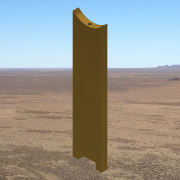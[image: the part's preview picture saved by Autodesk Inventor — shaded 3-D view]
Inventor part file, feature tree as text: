
AUTODESK INVENTOR PART (.ipt)
format: ipt  version: 2014 SP1 (Build 180222100, 222)  size: 161,792 bytes
history: native  units: in
note: dims shown in document units (in); Inventor stores cm internally (conversion verified against a paired STEP export)
features: sketch x5, extrude x3, hole x2, plane x1
ambient origin geometry x8: Origin, YZ Plane, XZ Plane, XY Plane, X Axis, Y Axis, Z Axis, Center Point
bodies: Solid1 (feature_tree)
feature tree (11):
  extrude  "Extrusion1"  Depth=3.06in
  extrude  "Extrusion2"  Depth=0.375in
  extrude  "Extrusion3"  TaperAngle=0.0deg  [1 undecoded]
  plane  "Work Plane1"
  hole  "Hole3"  [1 undecoded]
  hole  "Hole4"  [1 undecoded]
  sketch  "Sketch1"  dims[d0=3.06in d1=0.625in]
  sketch  "Sketch2"  dims[d2=0.125in d3=0.0in d4=0.375in]
  sketch  "Sketch3"  dims[d6=0.125in d7=0.0in d8=0.0in]
  sketch  "Sketch6"  dims[d9=0.125in d10=0.0in d11=0.875in]
  sketch  "Sketch7"  dims[d29=0.067in d30=1.2in d31=0.375in d32=0.25in d33=0.5635in d34=1.3in d35=0.8108in d36=0.625in d37=0.25in d38=0.067in d39=0.85in d40=0.375in d41=0.25in d42=0.5635in d43=1.0in d44=0.8108in]
note: 3 required parameter values undecoded (feature->parameter linkage not recoverable at this tier; creation-order binding heuristic only, values carry confidence <= 0.55)
